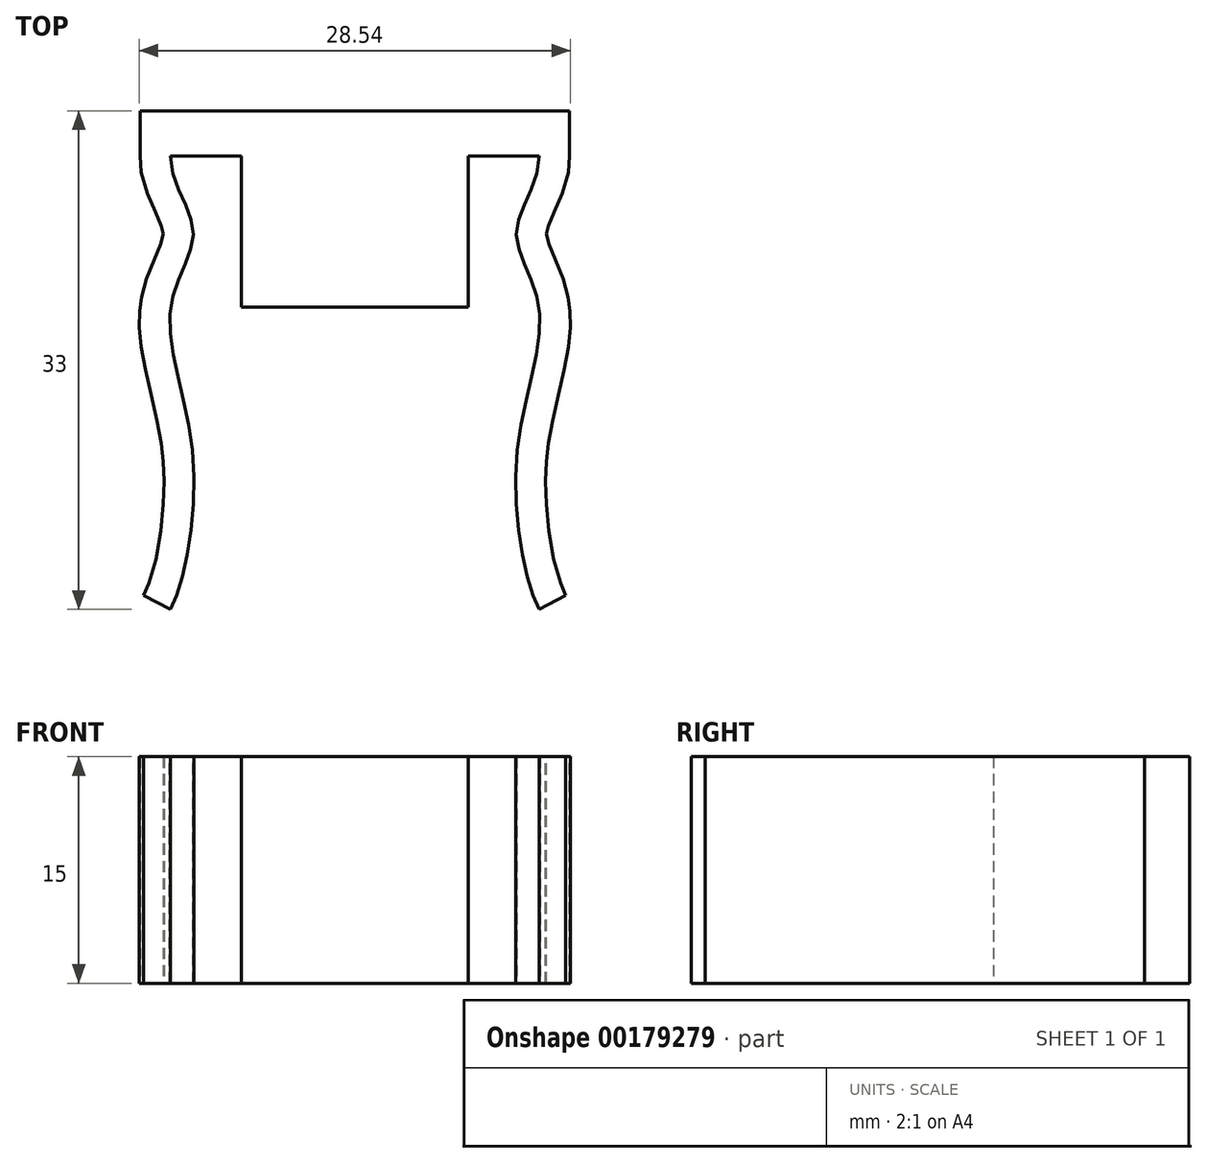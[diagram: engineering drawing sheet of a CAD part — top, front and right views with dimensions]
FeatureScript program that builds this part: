
annotation { "Feature Type Name" : "Feature", "Feature Type Description" : "" }
export const myFeature = defineFeature(function(context is Context, id is Id, definition is map)
    precondition{}
    {
        {
            var Q0;
            Q0=qCreatedBy(makeId("Top.planeOp"),FACE);
            var sketch = newSketch(context, id + "F0", { "sketchPlane" : qUnion([Q0])});
            skLineSegment(sketch, "E0", {"start": v(0, 0) * mm, "end": v(0, 31.35) * mm, "construction": true});
            skLineSegment(sketch, "E1.bottom", {"start": v(7.5, 10) * mm, "end": v(11.2, 10) * mm, "construction": true});
            skLineSegment(sketch, "E1.top", {"start": v(7.5, -20.52) * mm, "end": v(11.2, -20.52) * mm, "construction": true});
            skLineSegment(sketch, "E1.left", {"start": v(7.5, 10) * mm, "end": v(7.5, -20.52) * mm, "construction": true});
            skLineSegment(sketch, "E1.right", {"start": v(11.2, 10) * mm, "end": v(11.2, -20.52) * mm, "construction": true});
            skLineSegment(sketch, "E2", {"start": v(0, 0) * mm, "end": v(7.5, 0) * mm});
            skLineSegment(sketch, "E3", {"start": v(7.5, 0) * mm, "end": v(7.5, 10) * mm});
            skLineSegment(sketch, "E4", {"start": v(7.5, 10) * mm, "end": v(12.2, 10) * mm});
            skFitSpline(sketch, "E5", {"points": [v(12.2, 10) * mm, v(10.7, 5) * mm, v(12.2, 0) * mm, v(10.7, -10) * mm, v(12.2, -20) * mm], "startDerivative": vector(0, -26.98) * mm, "endDerivative": vector(9.14, -17.4) * mm});
            skPoint(sketch, "E6", {"position": v(7.5, 5) * mm});
            skLineSegment(sketch, "E7", {"start": v(12.2, 0) * mm, "end": v(12.2, -20) * mm, "construction": true});
            skPoint(sketch, "E8", {"position": v(12.2, -10) * mm});
            skFitSpline(sketch, "E9.0", {"points": [v(14.2, 10) * mm, v(14.2, 9.57) * mm, v(14.1, 8.75) * mm, v(13.79, 7.7) * mm, v(13.42, 6.81) * mm, v(13.08, 6.07) * mm, v(12.87, 5.57) * mm, v(12.76, 5.25) * mm, v(12.72, 5.07) * mm, v(12.7, 4.96) * mm, v(12.7, 4.9) * mm, v(12.7, 4.84) * mm, v(12.7, 4.73) * mm, v(12.75, 4.5) * mm, v(12.87, 4.1) * mm, v(13.14, 3.47) * mm, v(13.47, 2.7) * mm, v(13.82, 1.8) * mm, v(14.05, 1.01) * mm, v(14.16, 0.44) * mm, v(14.22, 0.05) * mm, v(14.26, -0.44) * mm, v(14.27, -1.02) * mm, v(14.23, -1.79) * mm, v(14.12, -2.73) * mm, v(13.92, -3.84) * mm, v(13.6, -5.31) * mm, v(13.24, -6.79) * mm, v(12.94, -8.27) * mm, v(12.8, -9.2) * mm, v(12.7, -9.95) * mm, v(12.65, -10.7) * mm, v(12.62, -11.66) * mm, v(12.66, -12.84) * mm, v(12.79, -14.4) * mm, v(13.08, -16.25) * mm, v(13.47, -17.78) * mm, v(13.78, -18.67) * mm, v(13.92, -18.97) * mm, v(13.97, -19.07) * mm]});
            skLineSegment(sketch, "E10", {"start": v(12.2, -20) * mm, "end": v(13.97, -19.07) * mm});
            skLineSegment(sketch, "E11", {"start": v(14.2, 10) * mm, "end": v(14.2, 13) * mm});
            skLineSegment(sketch, "E12", {"start": v(14.2, 13) * mm, "end": v(0, 13) * mm});
            skLineSegment(sketch, "E13", {"start": v(0, 13) * mm, "end": v(0, 0) * mm});
            skSolve(sketch);
        }
        {
            var Q0;
            Q0 = qSketchRegion(id + "F0", true);
            extrude(context, id + "F1", {"entities" : qUnion([Q0]), "depth" : 15 * mm, "offsetDistance" : 25 * mm});
        }
        {
            var Q0;
            Q0=makeQuery(id+"F1.opExtrude","SWEPT_BODY",BODY,{"disambiguationData":[OSD([sQuery(id+"F0.wireOp",EDGE,"E2"),sQuery(id+"F0.wireOp",EDGE,"E3"),sQuery(id+"F0.wireOp",EDGE,"E4"),sQuery(id+"F0.wireOp",EDGE,"E5"),sQuery(id+"F0.wireOp",EDGE,"E9.0"),sQuery(id+"F0.wireOp",EDGE,"E10"),sQuery(id+"F0.wireOp",EDGE,"E11"),sQuery(id+"F0.wireOp",EDGE,"E12"),sQuery(id+"F0.wireOp",EDGE,"E13")])]});
            var Q1;
            Q1=qCreatedBy(makeId("Right.planeOp"),FACE);
            mirror(context, id + "F2", {"operationType" : NewBodyOperationType.ADD, "entities" : qUnion([Q0]), "mirrorPlane" : qUnion([Q1])});
        }
    });
